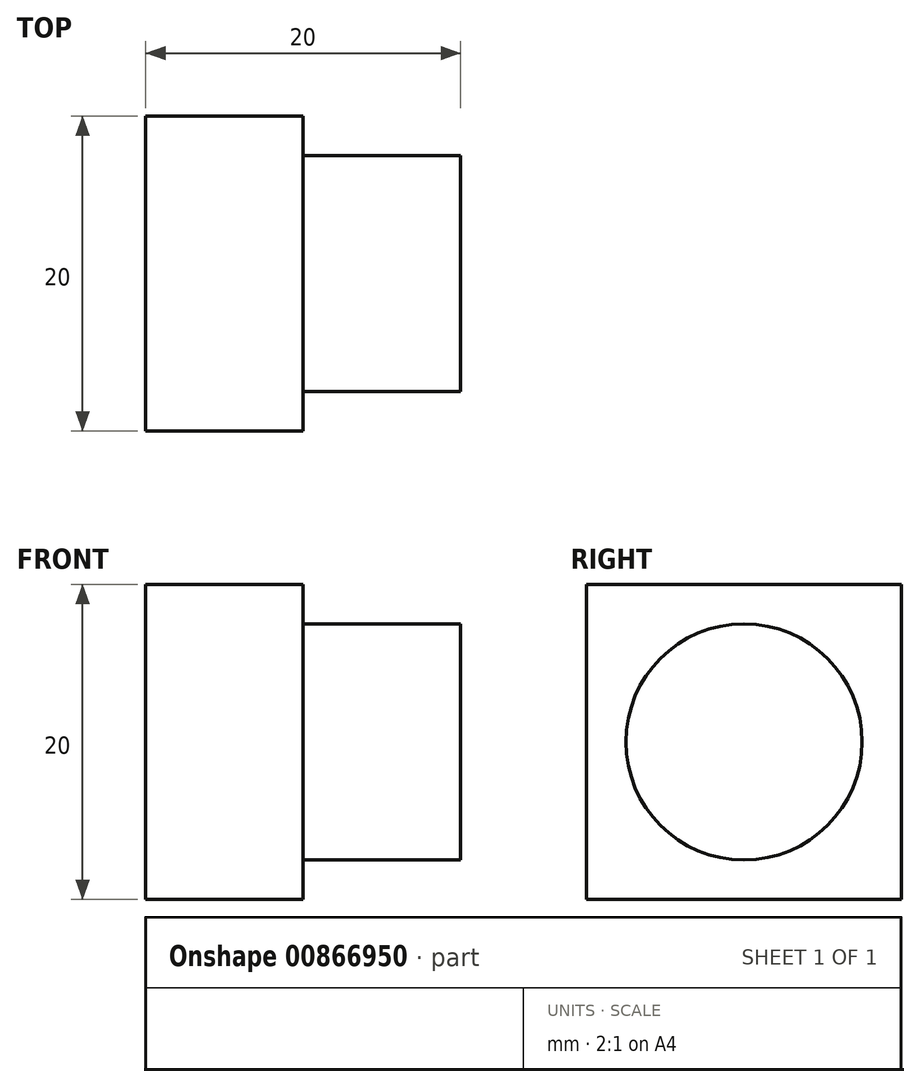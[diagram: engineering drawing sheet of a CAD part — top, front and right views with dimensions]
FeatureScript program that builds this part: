
annotation { "Feature Type Name" : "Feature", "Feature Type Description" : "" }
export const myFeature = defineFeature(function(context is Context, id is Id, definition is map)
    precondition{}
    {
        {
            var Q0;
            Q0=qCreatedBy(makeId("Right.planeOp"),FACE);
            var sketch = newSketch(context, id + "F0", { "sketchPlane" : qUnion([Q0])});
            skLineSegment(sketch, "E0.bottom", {"start": v(-10, -10) * mm, "end": v(10, -10) * mm});
            skLineSegment(sketch, "E0.top", {"start": v(-10, 10) * mm, "end": v(10, 10) * mm});
            skLineSegment(sketch, "E0.left", {"start": v(-10, -10) * mm, "end": v(-10, 10) * mm});
            skLineSegment(sketch, "E0.right", {"start": v(10, -10) * mm, "end": v(10, 10) * mm});
            skLineSegment(sketch, "E1", {"start": v(-10, 10) * mm, "end": v(10, -10) * mm, "construction": true});
            skSolve(sketch);
        }
        {
            var Q0;
            Q0 = qSketchRegion(id + "F0", true);
            extrude(context, id + "F1", {"entities" : qUnion([Q0]), "depth" : 10 * mm, "offsetDistance" : 25 * mm});
        }
        {
            var Q0;
            Q0=makeQuery(id+"F1.opExtrude","CAP_FACE",FACE,{"disambiguationData":[OSD([sQuery(id+"F0.wireOp",EDGE,"E0.bottom"),sQuery(id+"F0.wireOp",EDGE,"E0.top"),sQuery(id+"F0.wireOp",EDGE,"E0.left"),sQuery(id+"F0.wireOp",EDGE,"E0.right")])],"isStart":false});
            var sketch = newSketch(context, id + "F2", { "sketchPlane" : qUnion([Q0])});
            skCircle(sketch, "E2", {"center": v(0, 0) * mm, "radius": 7.5 * mm});
            skSolve(sketch);
        }
        {
            var Q0;
            Q0 = qSketchRegion(id + "F2", true);
            extrude(context, id + "F3", {"entities" : qUnion([Q0]), "operationType" : NewBodyOperationType.ADD, "depth" : 10 * mm, "offsetDistance" : 25 * mm});
        }
    });
